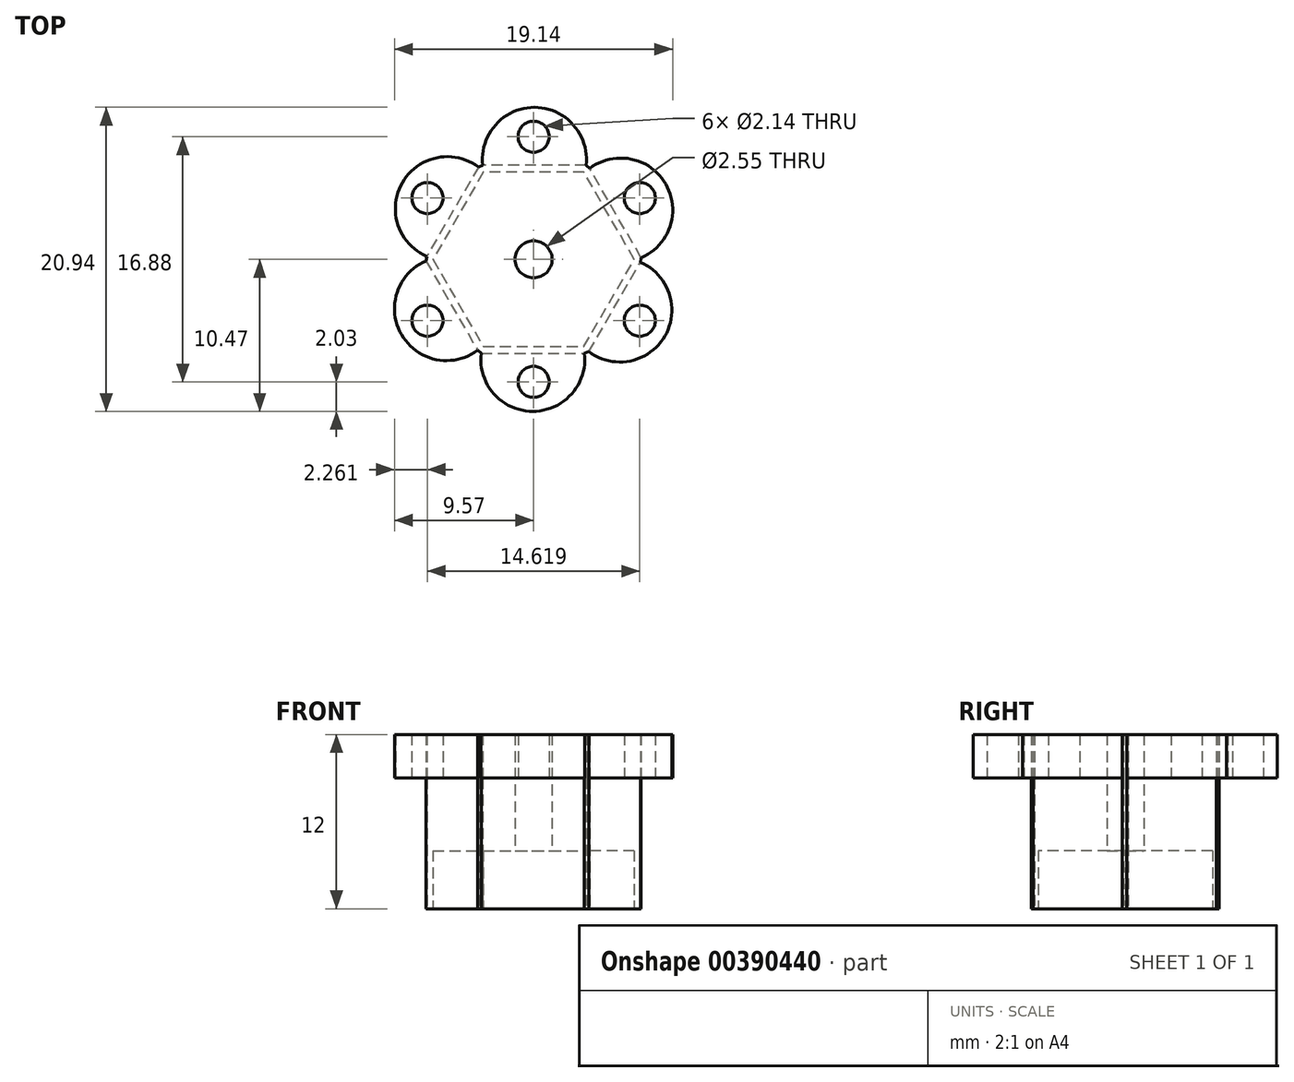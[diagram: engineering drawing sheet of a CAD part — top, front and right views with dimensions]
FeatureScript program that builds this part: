
annotation { "Feature Type Name" : "Feature", "Feature Type Description" : "" }
export const myFeature = defineFeature(function(context is Context, id is Id, definition is map)
    precondition{}
    {
        {
            var Q0;
            Q0=qCreatedBy(makeId("Top.planeOp"),FACE);
            var sketch = newSketch(context, id + "F0", { "sketchPlane" : qUnion([Q0])});
            skCircle(sketch, "E0.cCircle", {"center": v(0, 0) * mm, "radius": 6 * mm, "construction": true});
            skLineSegment(sketch, "E0.0", {"start": v(-6.93, 0.06) * mm, "end": v(-3.42, 6.03) * mm});
            skLineSegment(sketch, "E0.1", {"start": v(-3.42, 6.03) * mm, "end": v(3.51, 5.97) * mm});
            skLineSegment(sketch, "E0.2", {"start": v(3.51, 5.97) * mm, "end": v(6.93, -0.06) * mm});
            skLineSegment(sketch, "E0.3", {"start": v(6.93, -0.06) * mm, "end": v(3.42, -6.03) * mm});
            skLineSegment(sketch, "E0.4", {"start": v(3.42, -6.03) * mm, "end": v(-3.51, -5.97) * mm});
            skLineSegment(sketch, "E0.5", {"start": v(-3.51, -5.97) * mm, "end": v(-6.93, 0.06) * mm});
            skPoint(sketch, "E0.0.midPoint", {"position": v(-5.17, 3.04) * mm});
            skLineSegment(sketch, "E1", {"start": v(0, 0) * mm, "end": v(0, 8.44) * mm, "construction": true});
            skCircle(sketch, "E2", {"center": v(0, 8.44) * mm, "radius": 1.07 * mm});
            skCircle(sketch, "E3.1.0", {"center": v(-7.3, 4.22) * mm, "radius": 1.07 * mm});
            skCircle(sketch, "E3.2.0", {"center": v(-7.3, -4.22) * mm, "radius": 1.07 * mm});
            skCircle(sketch, "E3.3.0", {"center": v(0, -8.44) * mm, "radius": 1.07 * mm});
            skCircle(sketch, "E3.4.0", {"center": v(7.3, -4.22) * mm, "radius": 1.07 * mm});
            skCircle(sketch, "E3.5.0", {"center": v(7.3, 4.22) * mm, "radius": 1.07 * mm});
            skArc(sketch, "E4", {"start": v(-3.51, -5.97) * mm, "mid": v(-0.09, -10.47) * mm, "end": v(3.42, -6.03) * mm});
            skArc(sketch, "E5.1.0", {"start": v(3.42, -6.03) * mm, "mid": v(9.02, -5.3) * mm, "end": v(6.93, -0.06) * mm});
            skArc(sketch, "E5.2.0", {"start": v(6.93, -0.06) * mm, "mid": v(9.1, 5.16) * mm, "end": v(3.51, 5.97) * mm});
            skArc(sketch, "E5.3.0", {"start": v(3.51, 5.97) * mm, "mid": v(0.09, 10.47) * mm, "end": v(-3.42, 6.03) * mm});
            skArc(sketch, "E5.4.0", {"start": v(-3.42, 6.03) * mm, "mid": v(-9.02, 5.3) * mm, "end": v(-6.93, 0.06) * mm});
            skArc(sketch, "E5.5.0", {"start": v(-6.93, 0.06) * mm, "mid": v(-9.1, -5.16) * mm, "end": v(-3.51, -5.97) * mm});
            skSolve(sketch);
        }
        {
            var Q0;
            Q0 = qSketchRegion(id + "F0", true);
            extrude(context, id + "F1", {"entities" : qUnion([Q0]), "depth" : 12 * mm});
        }
        {
            var Q0;
            Q0=makeQuery(id+"F1.opExtrude","CAP_FACE",FACE,{"disambiguationData":[OSD([sQuery(id+"F0.wireOp",EDGE,"E2"),sQuery(id+"F0.wireOp",EDGE,"E3.1.0"),sQuery(id+"F0.wireOp",EDGE,"E3.2.0"),sQuery(id+"F0.wireOp",EDGE,"E3.3.0"),sQuery(id+"F0.wireOp",EDGE,"E3.4.0"),sQuery(id+"F0.wireOp",EDGE,"E3.5.0"),sQuery(id+"F0.wireOp",EDGE,"E4"),sQuery(id+"F0.wireOp",EDGE,"E5.1.0"),sQuery(id+"F0.wireOp",EDGE,"E5.2.0"),sQuery(id+"F0.wireOp",EDGE,"E5.3.0"),sQuery(id+"F0.wireOp",EDGE,"E5.4.0"),sQuery(id+"F0.wireOp",EDGE,"E5.5.0")])],"isStart":true});
            var sketch = newSketch(context, id + "F2", { "sketchPlane" : qUnion([Q0])});
            skCircle(sketch, "E6.cCircle", {"center": v(0, 0) * mm, "radius": 6 * mm, "construction": true});
            skLineSegment(sketch, "E6.0", {"start": v(-3.46, 6) * mm, "end": v(3.46, 6) * mm});
            skLineSegment(sketch, "E6.1", {"start": v(3.46, 6) * mm, "end": v(6.93, 0) * mm});
            skLineSegment(sketch, "E6.2", {"start": v(6.93, 0) * mm, "end": v(3.46, -6) * mm});
            skLineSegment(sketch, "E6.3", {"start": v(3.46, -6) * mm, "end": v(-3.46, -6) * mm});
            skLineSegment(sketch, "E6.4", {"start": v(-3.46, -6) * mm, "end": v(-6.93, 0) * mm});
            skLineSegment(sketch, "E6.5", {"start": v(-6.93, 0) * mm, "end": v(-3.46, 6) * mm});
            skPoint(sketch, "E6.0.midPoint", {"position": v(0, 6) * mm});
            skSolve(sketch);
        }
        {
            var Q0;
            Q0=makeQuery(id+"F2.imprint","IMPRINT",FACE,{"disambiguationData":[TD([[makeQuery(id+"F2.imprint","IMPRINT",EDGE,{"derivedFrom":sQuery(id+"F2.wireOp",EDGE,"E6.0")}),-1.0]])]});
            extrude(context, id + "F3", {"entities" : qUnion([Q0]), "operationType" : NewBodyOperationType.REMOVE, "oppositeDirection" : true, "depth" : 4 * mm});
        }
        {
            var Q0;
            Q0=makeQuery(id+"F3.boolean.opBoolean","COPY",FACE,{"derivedFrom":makeQuery(id+"F3.opExtrude","CAP_FACE",FACE,{"disambiguationData":[OSD([sQuery(id+"F2.wireOp",EDGE,"E6.0"),sQuery(id+"F2.wireOp",EDGE,"E6.1"),sQuery(id+"F2.wireOp",EDGE,"E6.2"),sQuery(id+"F2.wireOp",EDGE,"E6.3"),sQuery(id+"F2.wireOp",EDGE,"E6.4"),sQuery(id+"F2.wireOp",EDGE,"E6.5")])],"isStart":false})});
            var sketch = newSketch(context, id + "F4", { "sketchPlane" : qUnion([Q0])});
            skCircle(sketch, "E7", {"center": v(0, 0) * mm, "radius": 1.27 * mm});
            skSolve(sketch);
        }
        {
            var Q0;
            Q0 = qSketchRegion(id + "F4", true);
            extrude(context, id + "F5", {"entities" : qUnion([Q0]), "operationType" : NewBodyOperationType.REMOVE, "oppositeDirection" : true, "depth" : 25 * mm});
        }
        {
            var Q0;
            Q0=makeQuery(id+"F1.opExtrude","CAP_FACE",FACE,{"disambiguationData":[OSD([sQuery(id+"F0.wireOp",EDGE,"E2"),sQuery(id+"F0.wireOp",EDGE,"E3.1.0"),sQuery(id+"F0.wireOp",EDGE,"E3.2.0"),sQuery(id+"F0.wireOp",EDGE,"E3.3.0"),sQuery(id+"F0.wireOp",EDGE,"E3.4.0"),sQuery(id+"F0.wireOp",EDGE,"E3.5.0"),sQuery(id+"F0.wireOp",EDGE,"E4"),sQuery(id+"F0.wireOp",EDGE,"E5.1.0"),sQuery(id+"F0.wireOp",EDGE,"E5.2.0"),sQuery(id+"F0.wireOp",EDGE,"E5.3.0"),sQuery(id+"F0.wireOp",EDGE,"E5.4.0"),sQuery(id+"F0.wireOp",EDGE,"E5.5.0")])],"isStart":true});
            var sketch = newSketch(context, id + "F6", { "sketchPlane" : qUnion([Q0])});
            skLineSegment(sketch, "E8", {"start": v(-3.6, 6.47) * mm, "end": v(3.51, 6.47) * mm});
            skArc(sketch, "E9", {"start": v(3.51, 6.47) * mm, "mid": v(-0.05, 10.5) * mm, "end": v(-3.6, 6.47) * mm});
            skArc(sketch, "E10.1.0", {"start": v(-3.84, 6.28) * mm, "mid": v(-9.11, 5.2) * mm, "end": v(-7.4, 0.1) * mm});
            skLineSegment(sketch, "E10.1.1", {"start": v(-7.4, 0.1) * mm, "end": v(-3.84, 6.28) * mm});
            skArc(sketch, "E10.2.0", {"start": v(-7.36, -0.2) * mm, "mid": v(-9.06, -5.29) * mm, "end": v(-3.8, -6.36) * mm});
            skLineSegment(sketch, "E10.2.1", {"start": v(-3.8, -6.36) * mm, "end": v(-7.36, -0.2) * mm});
            skArc(sketch, "E10.3.0", {"start": v(-3.51, -6.47) * mm, "mid": v(0.05, -10.5) * mm, "end": v(3.6, -6.47) * mm});
            skLineSegment(sketch, "E10.3.1", {"start": v(3.6, -6.47) * mm, "end": v(-3.51, -6.47) * mm});
            skArc(sketch, "E10.4.0", {"start": v(3.84, -6.28) * mm, "mid": v(9.11, -5.2) * mm, "end": v(7.4, -0.1) * mm});
            skLineSegment(sketch, "E10.4.1", {"start": v(7.4, -0.1) * mm, "end": v(3.84, -6.28) * mm});
            skArc(sketch, "E10.5.0", {"start": v(7.36, 0.2) * mm, "mid": v(9.06, 5.29) * mm, "end": v(3.8, 6.36) * mm});
            skLineSegment(sketch, "E10.5.1", {"start": v(3.8, 6.36) * mm, "end": v(7.36, 0.2) * mm});
            skPoint(sketch, "E10.center", {"position": v(0, 0) * mm});
            skSolve(sketch);
        }
        {
            var Q0;
            Q0 = qSketchRegion(id + "F6", true);
            extrude(context, id + "F7", {"entities" : qUnion([Q0]), "operationType" : NewBodyOperationType.REMOVE, "oppositeDirection" : true, "depth" : 9 * mm});
        }
        {
            var Q0;
            Q0=makeQuery(id+"F1.opExtrude","CAP_FACE",FACE,{"disambiguationData":[OSD([sQuery(id+"F0.wireOp",EDGE,"E2"),sQuery(id+"F0.wireOp",EDGE,"E3.1.0"),sQuery(id+"F0.wireOp",EDGE,"E3.2.0"),sQuery(id+"F0.wireOp",EDGE,"E3.3.0"),sQuery(id+"F0.wireOp",EDGE,"E3.4.0"),sQuery(id+"F0.wireOp",EDGE,"E3.5.0"),sQuery(id+"F0.wireOp",EDGE,"E4"),sQuery(id+"F0.wireOp",EDGE,"E5.1.0"),sQuery(id+"F0.wireOp",EDGE,"E5.2.0"),sQuery(id+"F0.wireOp",EDGE,"E5.3.0"),sQuery(id+"F0.wireOp",EDGE,"E5.4.0"),sQuery(id+"F0.wireOp",EDGE,"E5.5.0")])],"isStart":true});
            var sketch = newSketch(context, id + "F8", { "sketchPlane" : qUnion([Q0])});
            skLineSegment(sketch, "E11", {"start": v(-3.6, 6.47) * mm, "end": v(-3.85, 6.26) * mm});
            skLineSegment(sketch, "E12", {"start": v(-3.85, 6.26) * mm, "end": v(-3.51, 5.97) * mm});
            skLineSegment(sketch, "E13", {"start": v(-3.51, 5.97) * mm, "end": v(-3.6, 6.47) * mm});
            skLineSegment(sketch, "E14.1.0", {"start": v(-7.35, -0.2) * mm, "end": v(-6.93, -0.06) * mm});
            skLineSegment(sketch, "E14.1.1", {"start": v(-7.4, 0.1) * mm, "end": v(-7.35, -0.2) * mm});
            skLineSegment(sketch, "E14.1.2", {"start": v(-6.93, -0.06) * mm, "end": v(-7.4, 0.1) * mm});
            skLineSegment(sketch, "E14.2.0", {"start": v(-3.5, -6.47) * mm, "end": v(-3.42, -6.03) * mm});
            skLineSegment(sketch, "E14.2.1", {"start": v(-3.8, -6.36) * mm, "end": v(-3.5, -6.47) * mm});
            skLineSegment(sketch, "E14.2.2", {"start": v(-3.42, -6.03) * mm, "end": v(-3.8, -6.36) * mm});
            skLineSegment(sketch, "E14.3.0", {"start": v(3.85, -6.26) * mm, "end": v(3.51, -5.97) * mm});
            skLineSegment(sketch, "E14.3.1", {"start": v(3.6, -6.47) * mm, "end": v(3.85, -6.26) * mm});
            skLineSegment(sketch, "E14.3.2", {"start": v(3.51, -5.97) * mm, "end": v(3.6, -6.47) * mm});
            skLineSegment(sketch, "E14.4.0", {"start": v(7.35, 0.2) * mm, "end": v(6.93, 0.06) * mm});
            skLineSegment(sketch, "E14.4.1", {"start": v(7.4, -0.1) * mm, "end": v(7.35, 0.2) * mm});
            skLineSegment(sketch, "E14.4.2", {"start": v(6.93, 0.06) * mm, "end": v(7.4, -0.1) * mm});
            skLineSegment(sketch, "E14.5.0", {"start": v(3.5, 6.47) * mm, "end": v(3.42, 6.03) * mm});
            skLineSegment(sketch, "E14.5.1", {"start": v(3.8, 6.36) * mm, "end": v(3.5, 6.47) * mm});
            skLineSegment(sketch, "E14.5.2", {"start": v(3.42, 6.03) * mm, "end": v(3.8, 6.36) * mm});
            skPoint(sketch, "E14.center", {"position": v(0, 0) * mm});
            skSolve(sketch);
        }
        {
            var Q0;
            Q0 = qSketchRegion(id + "F8", true);
            extrude(context, id + "F9", {"entities" : qUnion([Q0]), "operationType" : NewBodyOperationType.ADD, "oppositeDirection" : true, "depth" : 12 * mm});
        }
    });
